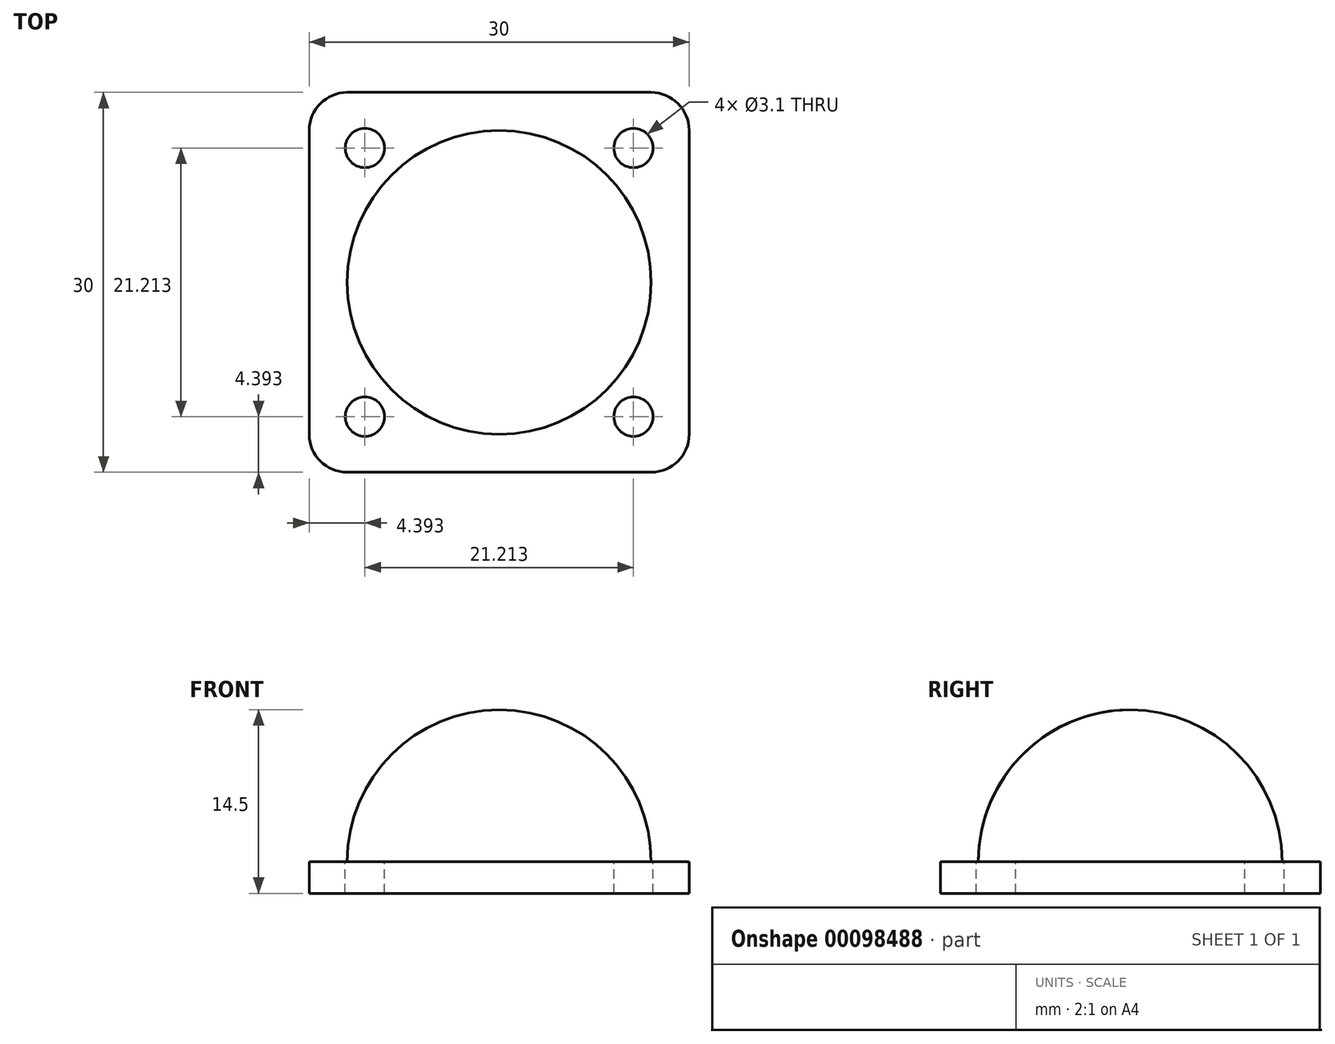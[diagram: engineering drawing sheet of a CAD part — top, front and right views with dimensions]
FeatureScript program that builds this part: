
annotation { "Feature Type Name" : "Feature", "Feature Type Description" : "" }
export const myFeature = defineFeature(function(context is Context, id is Id, definition is map)
    precondition{}
    {
        {
            var Q0;
            Q0=qCreatedBy(makeId("Right.planeOp"),FACE);
            var sketch = newSketch(context, id + "F0", { "sketchPlane" : qUnion([Q0])});
            skArc(sketch, "E0", {"start": v(-12, 0) * mm, "mid": v(-8.49, 8.49) * mm, "end": v(0, 12) * mm});
            skLineSegment(sketch, "E1", {"start": v(-12, 0) * mm, "end": v(0, 0) * mm});
            skLineSegment(sketch, "E2", {"start": v(0, 0) * mm, "end": v(0, 12) * mm});
            skPoint(sketch, "E3.orphan", {"position": v(12, 0) * mm});
            skSolve(sketch);
        }
        {
            var Q0;
            Q0=qSketchRegion(id+"F0",true);
            var Q1;
            Q1=sQuery(id+"F0.wireOp",EDGE,"E2");
            revolve(context, id + "F1", {"entities" : qUnion([Q0]), "axis" : qUnion([Q1]), "revolveType" : RevolveType.FULL});
        }
        {
            var Q0;
            Q0=makeQuery(id+"F1.opRevolve","SWEPT_FACE",FACE,{"disambiguationData":[OSD([sQuery(id+"F0.wireOp",EDGE,"E1")])]});
            var sketch = newSketch(context, id + "F2", { "sketchPlane" : qUnion([Q0])});
            skLineSegment(sketch, "E4.bottom", {"start": v(-15, -15) * mm, "end": v(15, -15) * mm});
            skLineSegment(sketch, "E4.top", {"start": v(-15, 15) * mm, "end": v(15, 15) * mm});
            skLineSegment(sketch, "E4.left", {"start": v(-15, -15) * mm, "end": v(-15, 15) * mm});
            skLineSegment(sketch, "E4.right", {"start": v(15, -15) * mm, "end": v(15, 15) * mm});
            skPoint(sketch, "E4.middle", {"position": v(0, 0) * mm});
            skCircle(sketch, "E5", {"center": v(0, 0) * mm, "radius": 15 * mm, "construction": true});
            skLineSegment(sketch, "E6", {"start": v(0, 0) * mm, "end": v(10.6, -10.6) * mm, "construction": true});
            skCircle(sketch, "E7", {"center": v(10.6, -10.6) * mm, "radius": 1.55 * mm});
            skCircle(sketch, "E8.1.0", {"center": v(10.6, 10.6) * mm, "radius": 1.55 * mm});
            skCircle(sketch, "E8.2.0", {"center": v(-10.6, 10.6) * mm, "radius": 1.55 * mm});
            skCircle(sketch, "E8.3.0", {"center": v(-10.6, -10.6) * mm, "radius": 1.55 * mm});
            skSolve(sketch);
        }
        {
            var Q0;
            Q0=makeQuery(id+"F2.imprint","IMPRINT",FACE,{"disambiguationData":[TD([[makeQuery(id+"F2.imprint","IMPRINT",EDGE,{"derivedFrom":sQuery(id+"F2.wireOp",EDGE,"E4.bottom")}),1.0]])]});
            var Q1;
            Q1=makeQuery(id+"F2.imprint","IMPRINT",FACE,{"disambiguationData":[TD([[makeQuery(id+"F2.imprint","IMPRINT",EDGE,{"derivedFrom":makeQuery(id+"F1.opRevolve","SWEPT_EDGE",EDGE,{"disambiguationData":[OSD([sQuery(id+"F0.wireOp",EDGE,"E0"),sQuery(id+"F0.wireOp",EDGE,"E1")])]})}),1.0]])]});
            extrude(context, id + "F3", {"entities" : qUnion([Q0, Q1]), "depth" : 2.5 * mm});
        }
        {
            var Q0;
            Q0=makeQuery(id+"F3.opExtrude","SWEPT_EDGE",EDGE,{"disambiguationData":[OSD([sQuery(id+"F2.wireOp",EDGE,"E4.bottom"),sQuery(id+"F2.wireOp",EDGE,"E4.right")])]});
            var Q1;
            Q1=makeQuery(id+"F3.opExtrude","SWEPT_EDGE",EDGE,{"disambiguationData":[OSD([sQuery(id+"F2.wireOp",EDGE,"E4.bottom"),sQuery(id+"F2.wireOp",EDGE,"E4.left")])]});
            var Q2;
            Q2=makeQuery(id+"F3.opExtrude","SWEPT_EDGE",EDGE,{"disambiguationData":[OSD([sQuery(id+"F2.wireOp",EDGE,"E4.top"),sQuery(id+"F2.wireOp",EDGE,"E4.right")])]});
            var Q3;
            Q3=makeQuery(id+"F3.opExtrude","SWEPT_EDGE",EDGE,{"disambiguationData":[OSD([sQuery(id+"F2.wireOp",EDGE,"E4.top"),sQuery(id+"F2.wireOp",EDGE,"E4.left")])]});
            fillet(context, id + "F4", {"entities" : qUnion([Q0, Q1, Q2, Q3]), "radius" : 3 * mm, "tangentPropagation" : true, "allowEdgeOverflow" : false});
        }
    });
